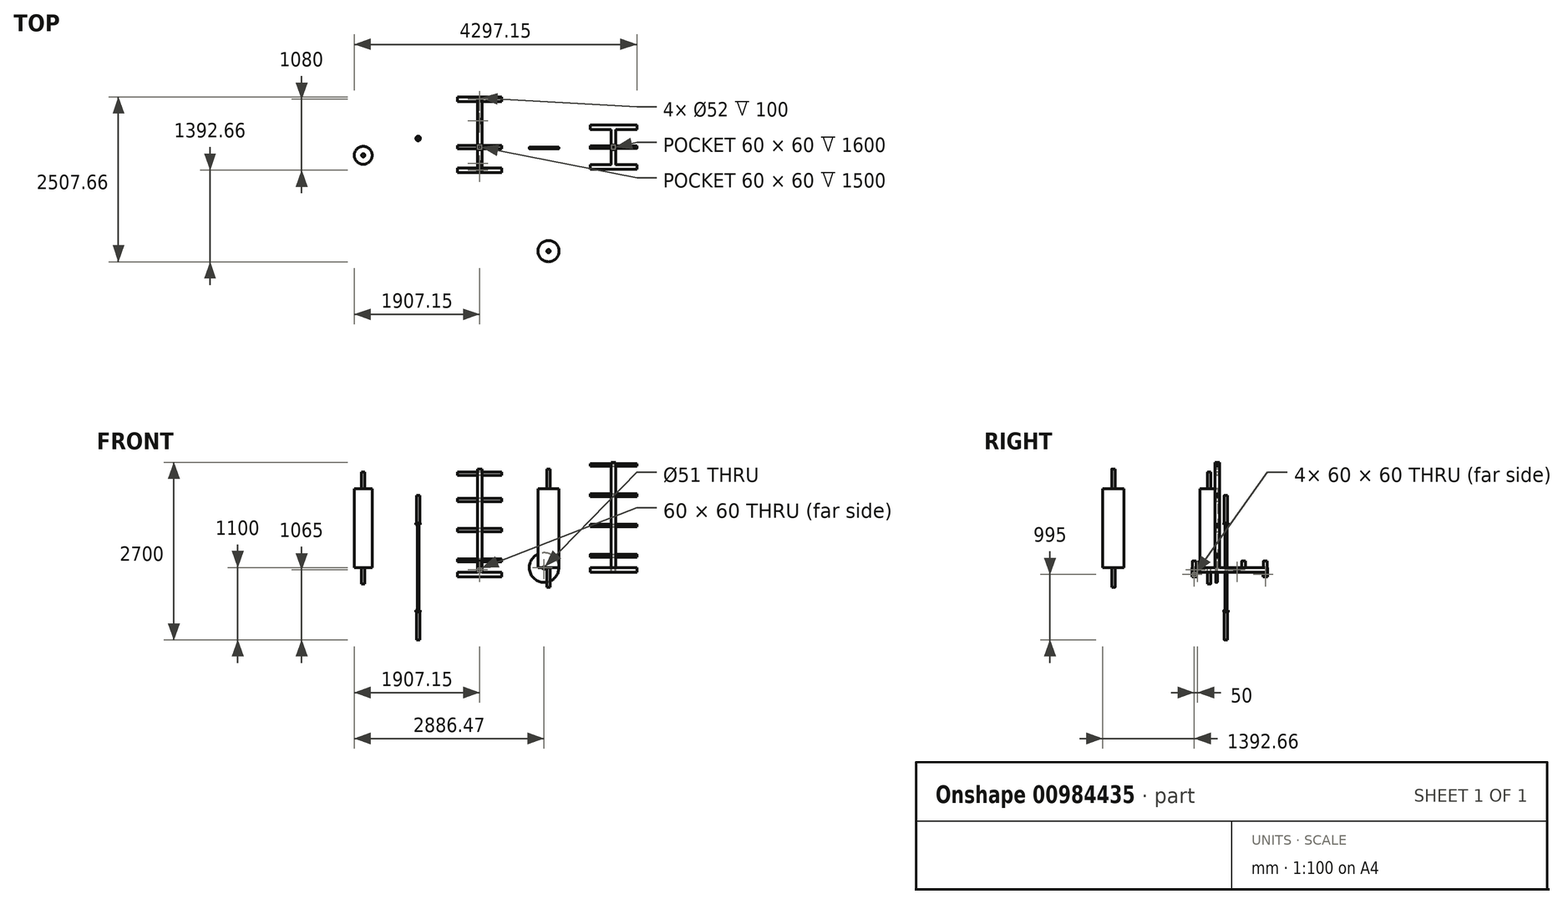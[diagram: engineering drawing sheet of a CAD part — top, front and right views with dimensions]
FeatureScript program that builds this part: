
annotation { "Feature Type Name" : "Feature", "Feature Type Description" : "" }
export const myFeature = defineFeature(function(context is Context, id is Id, definition is map)
    precondition{}
    {
        {
            var Q0;
            Q0=qCreatedBy(makeId("Top.planeOp"),FACE);
            var sketch = newSketch(context, id + "F0", { "sketchPlane" : qUnion([Q0])});
            skLineSegment(sketch, "E0.bottom", {"start": v(-30, 30) * mm, "end": v(30, 30) * mm});
            skLineSegment(sketch, "E0.top", {"start": v(-30, -30) * mm, "end": v(30, -30) * mm});
            skLineSegment(sketch, "E0.left", {"start": v(-30, 30) * mm, "end": v(-30, -30) * mm});
            skLineSegment(sketch, "E0.right", {"start": v(30, 30) * mm, "end": v(30, -30) * mm});
            skLineSegment(sketch, "E1.bottom", {"start": v(-35, 35) * mm, "end": v(35, 35) * mm});
            skLineSegment(sketch, "E1.top", {"start": v(-35, -35) * mm, "end": v(35, -35) * mm});
            skLineSegment(sketch, "E1.left", {"start": v(-35, 35) * mm, "end": v(-35, -35) * mm});
            skLineSegment(sketch, "E1.right", {"start": v(35, 35) * mm, "end": v(35, -35) * mm});
            skSolve(sketch);
        }
        {
            var Q0;
            Q0 = qSketchRegion(id + "F0", true);
            extrude(context, id + "F1", {"entities" : qUnion([Q0]), "depth" : 1500 * mm, "offsetDistance" : 25 * mm});
        }
        {
            var Q0;
            Q0=makeQuery(id+"F1.opExtrude","CAP_FACE",FACE,{"disambiguationData":[OSD([sQuery(id+"F0.wireOp",EDGE,"E0.bottom"),sQuery(id+"F0.wireOp",EDGE,"E0.top"),sQuery(id+"F0.wireOp",EDGE,"E0.left"),sQuery(id+"F0.wireOp",EDGE,"E0.right"),sQuery(id+"F0.wireOp",EDGE,"E1.bottom"),sQuery(id+"F0.wireOp",EDGE,"E1.top"),sQuery(id+"F0.wireOp",EDGE,"E1.left"),sQuery(id+"F0.wireOp",EDGE,"E1.right")])],"isStart":true});
            var sketch = newSketch(context, id + "F2", { "sketchPlane" : qUnion([Q0])});
            skLineSegment(sketch, "E2.bottom", {"start": v(-35, 385) * mm, "end": v(35, 385) * mm});
            skLineSegment(sketch, "E2.top", {"start": v(-35, -765) * mm, "end": v(35, -765) * mm});
            skLineSegment(sketch, "E2.left", {"start": v(-35, 385) * mm, "end": v(-35, -765) * mm});
            skLineSegment(sketch, "E2.right", {"start": v(35, 385) * mm, "end": v(35, -765) * mm});
            skSolve(sketch);
        }
        {
            var Q0;
            Q0 = qSketchRegion(id + "F2", true);
            extrude(context, id + "F3", {"entities" : qUnion([Q0]), "operationType" : NewBodyOperationType.ADD, "depth" : 70 * mm, "offsetDistance" : 25 * mm});
        }
        {
            var Q0;
            Q0=makeQuery(id+"F3.opExtrude","SWEPT_FACE",FACE,{"disambiguationData":[OSD([sQuery(id+"F2.wireOp",EDGE,"E2.top")])]});
            var sketch = newSketch(context, id + "F4", { "sketchPlane" : qUnion([Q0])});
            skLineSegment(sketch, "E3.bottom", {"start": v(-30, -5) * mm, "end": v(30, -5) * mm});
            skLineSegment(sketch, "E3.top", {"start": v(-30, -65) * mm, "end": v(30, -65) * mm});
            skLineSegment(sketch, "E3.left", {"start": v(-30, -5) * mm, "end": v(-30, -65) * mm});
            skLineSegment(sketch, "E3.right", {"start": v(30, -5) * mm, "end": v(30, -65) * mm});
            skSolve(sketch);
        }
        {
            var Q0;
            Q0 = qSketchRegion(id + "F4", true);
            extrude(context, id + "F5", {"entities" : qUnion([Q0]), "operationType" : NewBodyOperationType.REMOVE, "oppositeDirection" : true, "depth" : 1360 * mm, "offsetDistance" : 25 * mm});
        }
        {
            var Q0;
            Q0=makeQuery(id+"F3.opExtrude","CAP_FACE",FACE,{"disambiguationData":[OSD([sQuery(id+"F2.wireOp",EDGE,"E2.bottom"),sQuery(id+"F2.wireOp",EDGE,"E2.top"),sQuery(id+"F2.wireOp",EDGE,"E2.left"),sQuery(id+"F2.wireOp",EDGE,"E2.right")])],"isStart":false});
            var sketch = newSketch(context, id + "F6", { "sketchPlane" : qUnion([Q0])});
            skSolve(sketch);
        }
        {
            var Q0;
            Q0=makeQuery(id+"F6.imprint","IMPRINT",FACE,{"disambiguationData":[TD([[makeQuery(id+"F6.imprint","IMPRINT",EDGE,{"derivedFrom":makeQuery(id+"F3.opExtrude","CAP_EDGE",EDGE,{"disambiguationData":[OSD([sQuery(id+"F2.wireOp",EDGE,"E2.bottom")])],"isStart":false})}),-1.0]])]});
            var sketch = newSketch(context, id + "F7", { "sketchPlane" : qUnion([Q0])});
            skLineSegment(sketch, "E4.bottom", {"start": v(-335, 315) * mm, "end": v(335, 315) * mm});
            skLineSegment(sketch, "E4.top", {"start": v(-335, 385) * mm, "end": v(335, 385) * mm});
            skLineSegment(sketch, "E4.left", {"start": v(-335, 315) * mm, "end": v(-335, 385) * mm});
            skLineSegment(sketch, "E4.right", {"start": v(335, 315) * mm, "end": v(335, 385) * mm});
            skLineSegment(sketch, "E5.bottom", {"start": v(-335, -695) * mm, "end": v(335, -695) * mm});
            skLineSegment(sketch, "E5.top", {"start": v(-335, -765) * mm, "end": v(335, -765) * mm});
            skLineSegment(sketch, "E5.left", {"start": v(-335, -695) * mm, "end": v(-335, -765) * mm});
            skLineSegment(sketch, "E5.right", {"start": v(335, -695) * mm, "end": v(335, -765) * mm});
            skSolve(sketch);
        }
        {
            var Q0;
            Q0 = qSketchRegion(id + "F7", true);
            extrude(context, id + "F8", {"entities" : qUnion([Q0]), "operationType" : NewBodyOperationType.ADD, "depth" : 70 * mm, "offsetDistance" : 25 * mm});
        }
        {
            var Q0;
            Q0=makeQuery(id+"F8.opExtrude","SWEPT_FACE",FACE,{"disambiguationData":[OSD([sQuery(id+"F7.wireOp",EDGE,"E5.left")])]});
            var sketch = newSketch(context, id + "F9", { "sketchPlane" : qUnion([Q0])});
            skLineSegment(sketch, "E6.bottom", {"start": v(-700, -75) * mm, "end": v(-760, -75) * mm});
            skLineSegment(sketch, "E6.top", {"start": v(-700, -135) * mm, "end": v(-760, -135) * mm});
            skLineSegment(sketch, "E6.left", {"start": v(-700, -75) * mm, "end": v(-700, -135) * mm});
            skLineSegment(sketch, "E6.right", {"start": v(-760, -75) * mm, "end": v(-760, -135) * mm});
            skLineSegment(sketch, "E7.bottom", {"start": v(320, -75) * mm, "end": v(380, -75) * mm});
            skLineSegment(sketch, "E7.top", {"start": v(320, -135) * mm, "end": v(380, -135) * mm});
            skLineSegment(sketch, "E7.left", {"start": v(320, -75) * mm, "end": v(320, -135) * mm});
            skLineSegment(sketch, "E7.right", {"start": v(380, -75) * mm, "end": v(380, -135) * mm});
            skSolve(sketch);
        }
        {
            var Q0;
            Q0 = qSketchRegion(id + "F9", true);
            extrude(context, id + "F10", {"entities" : qUnion([Q0]), "operationType" : NewBodyOperationType.REMOVE, "oppositeDirection" : true, "depth" : 723 * mm, "offsetDistance" : 25 * mm});
        }
        {
            var Q0;
            {var subQ0=sQuery(id+"F2.wireOp",EDGE,"E2.bottom");var subQ1=sQuery(id+"F2.wireOp",EDGE,"E2.left");var subQ2=sQuery(id+"F2.wireOp",EDGE,"E2.right");Q0=makeQuery(id+"F3.boolean.opBoolean","SPLIT",FACE,{"disambiguationData":[TD([makeQuery(id+"F1.opExtrude","SWEPT_FACE",FACE,{"disambiguationData":[OSD([sQuery(id+"F0.wireOp",EDGE,"E1.top")])]})])],"derivedFrom":makeQuery(id+"F3.opExtrude","CAP_FACE",FACE,{"disambiguationData":[OSD([subQ0,sQuery(id+"F2.wireOp",EDGE,"E2.top"),subQ1,subQ2])],"isStart":true})});}
            var sketch = newSketch(context, id + "F11", { "sketchPlane" : qUnion([Q0])});
            skCircle(sketch, "E8", {"center": v(0, -250) * mm, "radius": 30 * mm});
            skCircle(sketch, "E9", {"center": v(0, -250) * mm, "radius": 26 * mm});
            skCircle(sketch, "E10", {"center": v(0, -350) * mm, "radius": 30 * mm});
            skCircle(sketch, "E11", {"center": v(0, -350) * mm, "radius": 26 * mm});
            skCircle(sketch, "E12", {"center": v(0, 730) * mm, "radius": 30 * mm});
            skCircle(sketch, "E13", {"center": v(0, 730) * mm, "radius": 26 * mm});
            skCircle(sketch, "E14", {"center": v(0, 400) * mm, "radius": 30 * mm});
            skCircle(sketch, "E15", {"center": v(0, 400) * mm, "radius": 26 * mm});
            skSolve(sketch);
        }
        {
            var Q0;
            Q0 = qSketchRegion(id + "F11", true);
            extrude(context, id + "F12", {"entities" : qUnion([Q0]), "operationType" : NewBodyOperationType.ADD, "depth" : 100 * mm, "offsetDistance" : 25 * mm});
        }
        {
            var Q0;
            Q0=makeQuery(id+"F3.boolean.opBoolean","MERGE",FACE,{"derivedFrom":[makeQuery(id+"F1.opExtrude","SWEPT_FACE",FACE,{"disambiguationData":[OSD([sQuery(id+"F0.wireOp",EDGE,"E1.left")])]}),makeQuery(id+"F3.opExtrude","SWEPT_FACE",FACE,{"disambiguationData":[OSD([sQuery(id+"F2.wireOp",EDGE,"E2.left")])]})]});
            var sketch = newSketch(context, id + "F13", { "sketchPlane" : qUnion([Q0])});
            skCircle(sketch, "E16", {"center": v(0, 110) * mm, "radius": 25 * mm});
            skCircle(sketch, "E17", {"center": v(0, 570) * mm, "radius": 25 * mm});
            skCircle(sketch, "E18", {"center": v(0, 1030) * mm, "radius": 25 * mm});
            skCircle(sketch, "E19", {"center": v(0, 1430) * mm, "radius": 25 * mm});
            skSolve(sketch);
        }
        {
            var Q0;
            Q0 = qSketchRegion(id + "F13", true);
            extrude(context, id + "F14", {"entities" : qUnion([Q0]), "operationType" : NewBodyOperationType.ADD, "depth" : 300 * mm, "offsetDistance" : 25 * mm});
        }
        {
            var Q0;
            Q0 = qSketchRegion(id + "F13", true);
            extrude(context, id + "F15", {"entities" : qUnion([Q0]), "operationType" : NewBodyOperationType.ADD, "oppositeDirection" : true, "depth" : 370 * mm, "offsetDistance" : 25 * mm});
        }
        {
            var Q0;
            Q0=qCreatedBy(makeId("Top.planeOp"),FACE);
            var sketch = newSketch(context, id + "F16", { "sketchPlane" : qUnion([Q0])});
            skCircle(sketch, "E20", {"center": v(-934.97, 131.93) * mm, "radius": 14 * mm});
            skSolve(sketch);
        }
        {
            var Q0;
            Q0 = qSketchRegion(id + "F16", true);
            extrude(context, id + "F17", {"entities" : qUnion([Q0]), "depth" : 650 * mm, "offsetDistance" : 25 * mm});
        }
        {
            var Q0;
            Q0=makeQuery(id+"F17.opExtrude","CAP_FACE",FACE,{"disambiguationData":[OSD([sQuery(id+"F16.wireOp",EDGE,"E20")])],"isStart":false});
            var sketch = newSketch(context, id + "F18", { "sketchPlane" : qUnion([Q0])});
            skCircle(sketch, "E21", {"center": v(-934.97, 131.93) * mm, "radius": 25 * mm});
            skSolve(sketch);
        }
        {
            var Q0;
            Q0 = qSketchRegion(id + "F18", true);
            extrude(context, id + "F19", {"entities" : qUnion([Q0]), "operationType" : NewBodyOperationType.ADD, "depth" : 450 * mm, "offsetDistance" : 25 * mm});
        }
        {
            var Q0;
            Q0=makeQuery(id+"F19.opExtrude","CAP_FACE",FACE,{"disambiguationData":[OSD([sQuery(id+"F18.wireOp",EDGE,"E21")])],"isStart":true});
            var sketch = newSketch(context, id + "F20", { "sketchPlane" : qUnion([Q0])});
            skCircle(sketch, "E22", {"center": v(-934.97, -131.93) * mm, "radius": 35 * mm});
            skSolve(sketch);
        }
        {
            var Q0;
            Q0 = qSketchRegion(id + "F20", true);
            extrude(context, id + "F21", {"entities" : qUnion([Q0]), "operationType" : NewBodyOperationType.ADD, "oppositeDirection" : true, "depth" : 25 * mm, "offsetDistance" : 25 * mm});
        }
        {
            var Q0;
            Q0 = qSketchRegion(id + "F16", true);
            extrude(context, id + "F22", {"entities" : qUnion([Q0]), "operationType" : NewBodyOperationType.ADD, "oppositeDirection" : true, "depth" : 650 * mm, "offsetDistance" : 25 * mm});
        }
        {
            var Q0;
            Q0=makeQuery(id+"F22.opExtrude","CAP_FACE",FACE,{"disambiguationData":[OSD([sQuery(id+"F16.wireOp",EDGE,"E20")])],"isStart":false});
            var sketch = newSketch(context, id + "F23", { "sketchPlane" : qUnion([Q0])});
            skCircle(sketch, "E23", {"center": v(-934.97, -131.93) * mm, "radius": 25 * mm});
            skSolve(sketch);
        }
        {
            var Q0;
            Q0 = qSketchRegion(id + "F23", true);
            extrude(context, id + "F24", {"entities" : qUnion([Q0]), "operationType" : NewBodyOperationType.ADD, "depth" : 450 * mm, "offsetDistance" : 25 * mm});
        }
        {
            var Q0;
            Q0=makeQuery(id+"F24.opExtrude","CAP_FACE",FACE,{"disambiguationData":[OSD([sQuery(id+"F23.wireOp",EDGE,"E23")])],"isStart":true});
            var sketch = newSketch(context, id + "F25", { "sketchPlane" : qUnion([Q0])});
            skCircle(sketch, "E24", {"center": v(-934.97, 131.93) * mm, "radius": 35 * mm});
            skSolve(sketch);
        }
        {
            var Q0;
            Q0 = qSketchRegion(id + "F25", true);
            extrude(context, id + "F26", {"entities" : qUnion([Q0]), "operationType" : NewBodyOperationType.ADD, "oppositeDirection" : true, "depth" : 25 * mm, "offsetDistance" : 25 * mm});
        }
        {
            var Q0;
            Q0=qCreatedBy(makeId("Front.planeOp"),FACE);
            var sketch = newSketch(context, id + "F27", { "sketchPlane" : qUnion([Q0])});
            skCircle(sketch, "E25", {"center": v(979.32, 0) * mm, "radius": 225 * mm});
            skCircle(sketch, "E26", {"center": v(979.32, 0) * mm, "radius": 25.5 * mm});
            skSolve(sketch);
        }
        {
            var Q0;
            Q0 = qSketchRegion(id + "F27", true);
            extrude(context, id + "F28", {"entities" : qUnion([Q0]), "depth" : 25 * mm, "offsetDistance" : 25 * mm});
        }
        {
            var Q0;
            Q0=makeQuery(id+"F28.opExtrude","CAP_EDGE",EDGE,{"disambiguationData":[OSD([sQuery(id+"F27.wireOp",EDGE,"E25")])],"isStart":true});
            var Q1;
            Q1=makeQuery(id+"F28.opExtrude","CAP_EDGE",EDGE,{"disambiguationData":[OSD([sQuery(id+"F27.wireOp",EDGE,"E25")])],"isStart":false});
            fillet(context, id + "F29", {"entities" : qUnion([Q0, Q1]), "radius" : 5 * mm, "tangentPropagation" : true, "allowEdgeOverflow" : false});
        }
        {
            var Q0;
            Q0=makeQuery(id+"F28.opExtrude","CAP_EDGE",EDGE,{"disambiguationData":[OSD([sQuery(id+"F27.wireOp",EDGE,"E26")])],"isStart":true});
            var Q1;
            Q1=makeQuery(id+"F28.opExtrude","CAP_EDGE",EDGE,{"disambiguationData":[OSD([sQuery(id+"F27.wireOp",EDGE,"E26")])],"isStart":false});
            fillet(context, id + "F30", {"entities" : qUnion([Q0, Q1]), "radius" : 2 * mm, "tangentPropagation" : true, "allowEdgeOverflow" : false});
        }
        {
            var Q0;
            Q0=qCreatedBy(makeId("Top.planeOp"),FACE);
            var sketch = newSketch(context, id + "F31", { "sketchPlane" : qUnion([Q0])});
            skCircle(sketch, "E27", {"center": v(-1770.65, -124.74) * mm, "radius": 136.5 * mm});
            skSolve(sketch);
        }
        {
            var Q0;
            Q0 = qSketchRegion(id + "F31", true);
            extrude(context, id + "F32", {"entities" : qUnion([Q0]), "depth" : 1200 * mm, "offsetDistance" : 25 * mm});
        }
        {
            var Q0;
            Q0=makeQuery(id+"F32.opExtrude","CAP_FACE",FACE,{"disambiguationData":[OSD([sQuery(id+"F31.wireOp",EDGE,"E27")])],"isStart":false});
            var sketch = newSketch(context, id + "F33", { "sketchPlane" : qUnion([Q0])});
            skCircle(sketch, "E28", {"center": v(-1770.65, -124.74) * mm, "radius": 25 * mm});
            skSolve(sketch);
        }
        {
            var Q0;
            Q0 = qSketchRegion(id + "F33", true);
            extrude(context, id + "F34", {"entities" : qUnion([Q0]), "operationType" : NewBodyOperationType.ADD, "depth" : 250 * mm, "offsetDistance" : 25 * mm});
        }
        {
            var Q0;
            Q0 = qSketchRegion(id + "F33", true);
            extrude(context, id + "F35", {"entities" : qUnion([Q0]), "operationType" : NewBodyOperationType.ADD, "oppositeDirection" : true, "depth" : 1450 * mm, "offsetDistance" : 25 * mm});
        }
        {
            var Q0;
            Q0=qCreatedBy(makeId("Top.planeOp"),FACE);
            var sketch = newSketch(context, id + "F36", { "sketchPlane" : qUnion([Q0])});
            skLineSegment(sketch, "E29.bottom", {"start": v(2000, 35) * mm, "end": v(2070, 35) * mm});
            skLineSegment(sketch, "E29.top", {"start": v(2000, -35) * mm, "end": v(2070, -35) * mm});
            skLineSegment(sketch, "E29.left", {"start": v(2000, 35) * mm, "end": v(2000, -35) * mm});
            skLineSegment(sketch, "E29.right", {"start": v(2070, 35) * mm, "end": v(2070, -35) * mm});
            skSolve(sketch);
        }
        {
            var Q0;
            Q0 = qSketchRegion(id + "F36", true);
            extrude(context, id + "F37", {"entities" : qUnion([Q0]), "depth" : 1600 * mm, "offsetDistance" : 25 * mm});
        }
        {
            var Q0;
            Q0=makeQuery(id+"F37.opExtrude","CAP_FACE",FACE,{"disambiguationData":[OSD([sQuery(id+"F36.wireOp",EDGE,"E29.bottom"),sQuery(id+"F36.wireOp",EDGE,"E29.top"),sQuery(id+"F36.wireOp",EDGE,"E29.left"),sQuery(id+"F36.wireOp",EDGE,"E29.right")])],"isStart":false});
            var Q1;
            Q1=makeQuery(id+"F37.opExtrude","CAP_FACE",FACE,{"disambiguationData":[OSD([sQuery(id+"F36.wireOp",EDGE,"E29.bottom"),sQuery(id+"F36.wireOp",EDGE,"E29.top"),sQuery(id+"F36.wireOp",EDGE,"E29.left"),sQuery(id+"F36.wireOp",EDGE,"E29.right")])],"isStart":true});
            shell(context, id + "F38", {"entities" : qUnion([Q0, Q1]), "thickness" : 5 * mm});
        }
        {
            var Q0;
            Q0=makeQuery(id+"F37.opExtrude","CAP_FACE",FACE,{"disambiguationData":[OSD([sQuery(id+"F36.wireOp",EDGE,"E29.bottom"),sQuery(id+"F36.wireOp",EDGE,"E29.top"),sQuery(id+"F36.wireOp",EDGE,"E29.left"),sQuery(id+"F36.wireOp",EDGE,"E29.right")])],"isStart":true});
            var sketch = newSketch(context, id + "F39", { "sketchPlane" : qUnion([Q0])});
            skLineSegment(sketch, "E30.bottom", {"start": v(2000, 265) * mm, "end": v(2070, 265) * mm});
            skLineSegment(sketch, "E30.top", {"start": v(2000, -265) * mm, "end": v(2070, -265) * mm});
            skLineSegment(sketch, "E30.left", {"start": v(2000, 265) * mm, "end": v(2000, -265) * mm});
            skLineSegment(sketch, "E30.right", {"start": v(2070, 265) * mm, "end": v(2070, -265) * mm});
            skLineSegment(sketch, "E31.bottom", {"start": v(1680, 335) * mm, "end": v(2390, 335) * mm});
            skLineSegment(sketch, "E31.top", {"start": v(1680, 265) * mm, "end": v(2390, 265) * mm});
            skLineSegment(sketch, "E31.left", {"start": v(1680, 335) * mm, "end": v(1680, 265) * mm});
            skLineSegment(sketch, "E31.right", {"start": v(2390, 335) * mm, "end": v(2390, 265) * mm});
            skLineSegment(sketch, "E32.bottom", {"start": v(1680, -335) * mm, "end": v(2390, -335) * mm});
            skLineSegment(sketch, "E32.top", {"start": v(1680, -265) * mm, "end": v(2390, -265) * mm});
            skLineSegment(sketch, "E32.left", {"start": v(1680, -335) * mm, "end": v(1680, -265) * mm});
            skLineSegment(sketch, "E32.right", {"start": v(2390, -335) * mm, "end": v(2390, -265) * mm});
            skSolve(sketch);
        }
        {
            var Q0;
            Q0 = qSketchRegion(id + "F39", true);
            extrude(context, id + "F40", {"entities" : qUnion([Q0]), "operationType" : NewBodyOperationType.ADD, "depth" : 70 * mm, "offsetDistance" : 25 * mm});
        }
        {
            var Q0;
            Q0=makeQuery(id+"F40.opExtrude","SWEPT_FACE",FACE,{"disambiguationData":[OSD([sQuery(id+"F39.wireOp",EDGE,"E31.right")])]});
            var Q1;
            Q1=makeQuery(id+"F40.opExtrude","SWEPT_FACE",FACE,{"disambiguationData":[OSD([sQuery(id+"F39.wireOp",EDGE,"E32.right")])]});
            var Q2;
            Q2=makeQuery(id+"F40.opExtrude","SWEPT_FACE",FACE,{"disambiguationData":[OSD([sQuery(id+"F39.wireOp",EDGE,"E32.left")])]});
            var Q3;
            Q3=makeQuery(id+"F40.opExtrude","SWEPT_FACE",FACE,{"disambiguationData":[OSD([sQuery(id+"F39.wireOp",EDGE,"E31.left")])]});
            shell(context, id + "F41", {"entities" : qUnion([Q0, Q1, Q2, Q3]), "thickness" : 5 * mm});
        }
        {
            var Q0;
            Q0=makeQuery(id+"F40.boolean.opBoolean","MERGE",FACE,{"derivedFrom":[makeQuery(id+"F37.opExtrude","SWEPT_FACE",FACE,{"disambiguationData":[OSD([sQuery(id+"F36.wireOp",EDGE,"E29.right")])]}),makeQuery(id+"F40.opExtrude","SWEPT_FACE",FACE,{"disambiguationData":[OSD([sQuery(id+"F39.wireOp",EDGE,"E30.right")])]})]});
            var sketch = newSketch(context, id + "F42", { "sketchPlane" : qUnion([Q0])});
            skCircle(sketch, "E33", {"center": v(0, 180) * mm, "radius": 20 * mm});
            skCircle(sketch, "E34", {"center": v(0, 640) * mm, "radius": 20 * mm});
            skCircle(sketch, "E35", {"center": v(0, 1100) * mm, "radius": 20 * mm});
            skCircle(sketch, "E36", {"center": v(0, 1560) * mm, "radius": 20 * mm});
            skSolve(sketch);
        }
        {
            var Q0;
            Q0 = qSketchRegion(id + "F42", true);
            extrude(context, id + "F43", {"entities" : qUnion([Q0]), "operationType" : NewBodyOperationType.ADD, "depth" : 320 * mm, "offsetDistance" : 25 * mm});
        }
        {
            var Q0;
            Q0 = qSketchRegion(id + "F42", true);
            extrude(context, id + "F44", {"entities" : qUnion([Q0]), "operationType" : NewBodyOperationType.ADD, "oppositeDirection" : true, "depth" : 390 * mm, "offsetDistance" : 25 * mm});
        }
        {
            var Q0;
            Q0=qCreatedBy(makeId("Top.planeOp"),FACE);
            var sketch = newSketch(context, id + "F45", { "sketchPlane" : qUnion([Q0])});
            skCircle(sketch, "E37", {"center": v(1047.12, -1581.16) * mm, "radius": 161.5 * mm});
            skSolve(sketch);
        }
        {
            var Q0;
            Q0 = qSketchRegion(id + "F45", true);
            extrude(context, id + "F46", {"entities" : qUnion([Q0]), "depth" : 1200 * mm, "offsetDistance" : 25 * mm});
        }
        {
            var Q0;
            Q0=makeQuery(id+"F46.opExtrude","CAP_FACE",FACE,{"disambiguationData":[OSD([sQuery(id+"F45.wireOp",EDGE,"E37")])],"isStart":false});
            var sketch = newSketch(context, id + "F47", { "sketchPlane" : qUnion([Q0])});
            skCircle(sketch, "E38", {"center": v(1047.12, -1581.16) * mm, "radius": 25 * mm});
            skSolve(sketch);
        }
        {
            var Q0;
            Q0 = qSketchRegion(id + "F47", true);
            extrude(context, id + "F48", {"entities" : qUnion([Q0]), "operationType" : NewBodyOperationType.ADD, "depth" : 300 * mm, "offsetDistance" : 25 * mm});
        }
        {
            var Q0;
            Q0 = qSketchRegion(id + "F47", true);
            extrude(context, id + "F49", {"entities" : qUnion([Q0]), "operationType" : NewBodyOperationType.ADD, "oppositeDirection" : true, "depth" : 1500 * mm, "offsetDistance" : 25 * mm});
        }
    });
